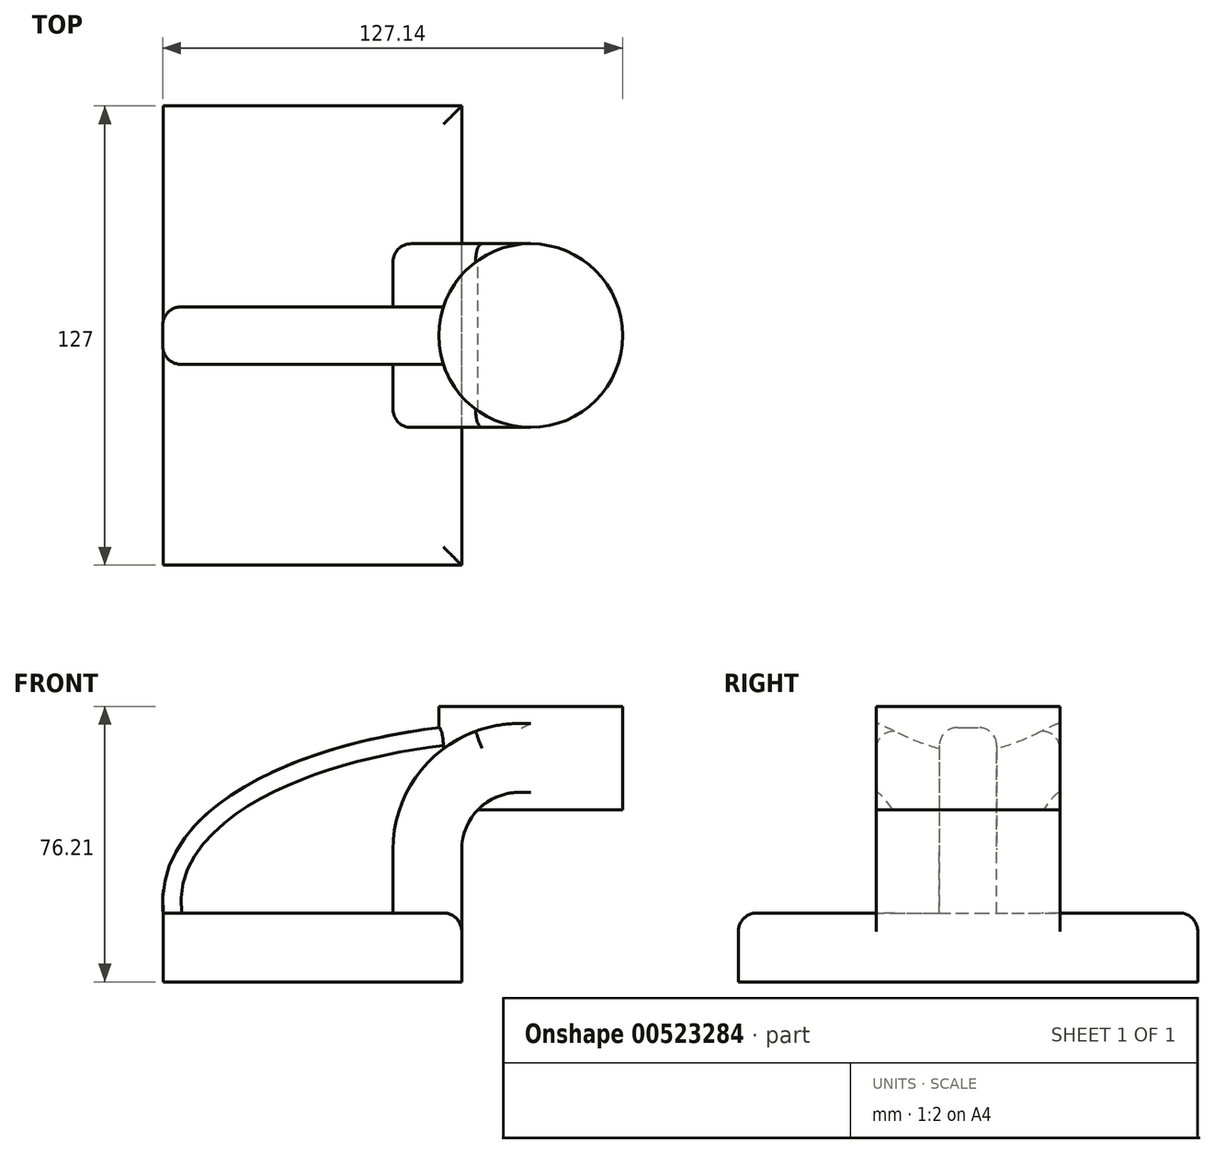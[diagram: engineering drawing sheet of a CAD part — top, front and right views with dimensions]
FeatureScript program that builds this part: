
annotation { "Feature Type Name" : "Feature", "Feature Type Description" : "" }
export const myFeature = defineFeature(function(context is Context, id is Id, definition is map)
    precondition{}
    {
        {
            var Q0;
            Q0=qCreatedBy(makeId("Front.planeOp"),FACE);
            var sketch = newSketch(context, id + "F0", { "sketchPlane" : qUnion([Q0])});
            skLineSegment(sketch, "E0.bottom", {"start": v(-41.28, -9.52) * mm, "end": v(41.28, -9.52) * mm});
            skLineSegment(sketch, "E0.top", {"start": v(-41.28, 9.53) * mm, "end": v(41.28, 9.53) * mm});
            skLineSegment(sketch, "E0.left", {"start": v(-41.27, -9.52) * mm, "end": v(-41.28, 9.53) * mm});
            skLineSegment(sketch, "E0.right", {"start": v(41.28, -9.52) * mm, "end": v(41.28, 9.53) * mm});
            skPoint(sketch, "E0.middle", {"position": v(0, 0) * mm});
            skLineSegment(sketch, "E1.bottom", {"start": v(60.32, 38.1) * mm, "end": v(111.12, 38.1) * mm});
            skLineSegment(sketch, "E1.top", {"start": v(60.32, 66.68) * mm, "end": v(111.12, 66.68) * mm});
            skLineSegment(sketch, "E1.left", {"start": v(60.32, 38.1) * mm, "end": v(60.32, 66.67) * mm});
            skLineSegment(sketch, "E1.right", {"start": v(111.13, 38.1) * mm, "end": v(111.12, 66.67) * mm});
            skPoint(sketch, "E1.middle", {"position": v(85.72, 52.39) * mm});
            skLineSegment(sketch, "E2", {"start": v(41.27, 9.53) * mm, "end": v(41.27, 27) * mm});
            skArc(sketch, "E3", {"start": v(57.15, 42.88) * mm, "mid": v(45.92, 38.23) * mm, "end": v(41.27, 27) * mm});
            skLineSegment(sketch, "E4", {"start": v(57.15, 42.88) * mm, "end": v(85.72, 42.88) * mm});
            skLineSegment(sketch, "E5.0", {"start": v(22.23, 9.53) * mm, "end": v(22.23, 27) * mm});
            skArc(sketch, "E5.1", {"start": v(57.15, 61.93) * mm, "mid": v(32.45, 51.7) * mm, "end": v(22.22, 27) * mm});
            skLineSegment(sketch, "E5.2", {"start": v(57.15, 61.93) * mm, "end": v(85.72, 61.93) * mm});
            skLineSegment(sketch, "E6", {"start": v(85.72, 61.93) * mm, "end": v(85.72, 52.39) * mm});
            skLineSegment(sketch, "E7", {"start": v(85.72, 52.39) * mm, "end": v(85.72, 42.88) * mm});
            skLineSegment(sketch, "E8", {"start": v(85.72, 66.68) * mm, "end": v(85.72, 38.1) * mm});
            skFitSpline(sketch, "E9", {"points": [v(-41.28, 9.53) * mm, v(57.15, 61.93) * mm], "startDerivative": vector(-10.2, 109.99) * mm, "endDerivative": vector(117.62, -2.77) * mm});
            skSolve(sketch);
        }
        {
            var Q0;
            Q0=makeQuery(id+"F0.imprint","IMPRINT",FACE,{"disambiguationData":[TD([[makeQuery(id+"F0.imprint","IMPRINT",EDGE,{"derivedFrom":sQuery(id+"F0.wireOp",EDGE,"E0.bottom")}),1.0]])]});
            extrude(context, id + "F1", {"entities" : qUnion([Q0]), "endBound" : BoundingType.SYMMETRIC, "depth" : 127 * mm, "offsetDistance" : 25.4 * mm});
        }
        {
            var Q0;
            {var subQ1=sQuery(id+"F0.wireOp",EDGE,"E2");Q0=makeQuery(id+"F0.imprint","IMPRINT",FACE,{"disambiguationData":[TD([[makeQuery(id+"F0.imprint","IMPRINT",EDGE,{"derivedFrom":subQ1}),1.0]])]});}
            extrude(context, id + "F2", {"entities" : qUnion([Q0]), "operationType" : NewBodyOperationType.ADD, "endBound" : BoundingType.SYMMETRIC, "depth" : 50.8 * mm, "offsetDistance" : 25.4 * mm});
        }
        {
            var Q0;
            {var subQ2=sQuery(id+"F0.wireOp",EDGE,"E5.0");Q0=makeQuery(id+"F0.imprint","IMPRINT",FACE,{"disambiguationData":[TD([[makeQuery(id+"F0.imprint","IMPRINT",EDGE,{"derivedFrom":subQ2}),1.0]])]});}
            extrude(context, id + "F3", {"entities" : qUnion([Q0]), "operationType" : NewBodyOperationType.ADD, "endBound" : BoundingType.SYMMETRIC, "depth" : 15.88 * mm, "offsetDistance" : 25.4 * mm});
        }
        {
            var Q0;
            {var subQ0=sQuery(id+"F0.wireOp",EDGE,"E1.left");var subQ1=sQuery(id+"F0.wireOp",EDGE,"E1.top");var subQ2=makeQuery(id+"F0.imprint","INTERSECT",VERTEX,{"derivedFrom":[subQ1,subQ0]});Q0=makeQuery(id+"F0.imprint","IMPRINT",FACE,{"disambiguationData":[TD([[makeQuery(id+"F0.imprint","IMPRINT",EDGE,{"disambiguationData":[TD([[subQ2,-1.0]])],"derivedFrom":subQ1}),-1.0]])]});}
            var Q1;
            {var subQ0=sQuery(id+"F0.wireOp",EDGE,"E4");var subQ1=sQuery(id+"F0.wireOp",EDGE,"E1.left");var subQ2=makeQuery(id+"F0.imprint","INTERSECT",VERTEX,{"derivedFrom":[subQ1,subQ0]});Q1=makeQuery(id+"F0.imprint","IMPRINT",FACE,{"disambiguationData":[TD([[makeQuery(id+"F0.imprint","IMPRINT",EDGE,{"disambiguationData":[TD([[subQ2,-1.0]])],"derivedFrom":subQ1}),-1.0]])]});}
            var Q2;
            {var subQ0=sQuery(id+"F0.wireOp",EDGE,"E1.left");var subQ1=sQuery(id+"F0.wireOp",EDGE,"E1.bottom");var subQ2=makeQuery(id+"F0.imprint","INTERSECT",VERTEX,{"derivedFrom":[subQ1,subQ0]});Q2=makeQuery(id+"F0.imprint","IMPRINT",FACE,{"disambiguationData":[TD([[makeQuery(id+"F0.imprint","IMPRINT",EDGE,{"disambiguationData":[TD([[subQ2,-1.0]])],"derivedFrom":subQ1}),1.0]])]});}
            var Q3;
            Q3=sQuery(id+"F0.wireOp",EDGE,"E1.left");
            revolve(context, id + "F4", {"operationType" : NewBodyOperationType.ADD, "entities" : qUnion([Q0, Q1, Q2]), "axis" : qUnion([Q3]), "revolveType" : RevolveType.FULL});
        }
        {
            var Q0;
            Q0=makeQuery(id+"F3.opExtrude","CAP_EDGE",EDGE,{"disambiguationData":[OSD([sQuery(id+"F0.wireOp",EDGE,"E9")])],"isStart":false});
            var Q1;
            Q1=makeQuery(id+"F3.opExtrude","CAP_EDGE",EDGE,{"disambiguationData":[OSD([sQuery(id+"F0.wireOp",EDGE,"E9")])],"isStart":true});
            var Q2;
            Q2=makeQuery(id+"F2.opExtrude","CAP_EDGE",EDGE,{"disambiguationData":[OSD([sQuery(id+"F0.wireOp",EDGE,"E5.1")])],"isStart":true});
            var Q3;
            Q3=makeQuery(id+"F2.opExtrude","CAP_EDGE",EDGE,{"disambiguationData":[OSD([sQuery(id+"F0.wireOp",EDGE,"E5.0")])],"isStart":true});
            var Q4;
            Q4=makeQuery(id+"F2.opExtrude","CAP_EDGE",EDGE,{"disambiguationData":[OSD([sQuery(id+"F0.wireOp",EDGE,"E5.1")])],"isStart":false});
            var Q5;
            Q5=makeQuery(id+"F2.opExtrude","CAP_EDGE",EDGE,{"disambiguationData":[OSD([sQuery(id+"F0.wireOp",EDGE,"E5.0")])],"isStart":false});
            fillet(context, id + "F5", {"entities" : qUnion([Q0, Q1, Q2, Q3, Q4, Q5]), "radius" : 5.08 * mm, "tangentPropagation" : true, "allowEdgeOverflow" : false});
        }
        {
            var Q0;
            {var subQ0=sQuery(id+"F0.wireOp",EDGE,"E2");var subQ1=sQuery(id+"F0.wireOp",EDGE,"E0.top");var subQ2=sQuery(id+"F0.wireOp",EDGE,"E0.right");Q0=makeQuery(id+"F2.boolean.opBoolean","SPLIT",EDGE,{"disambiguationData":[TD([makeQuery(id+"F1.opExtrude","CAP_FACE",FACE,{"disambiguationData":[OSD([sQuery(id+"F0.wireOp",EDGE,"E0.bottom"),subQ1,sQuery(id+"F0.wireOp",EDGE,"E0.left"),subQ2])],"isStart":true})])],"derivedFrom":makeQuery(id+"F1.opExtrude","SWEPT_EDGE",EDGE,{"disambiguationData":[OSD([subQ1,subQ2,subQ0])]})});}
            var Q1;
            Q1=makeQuery(id+"F1.opExtrude","CAP_EDGE",EDGE,{"disambiguationData":[OSD([sQuery(id+"F0.wireOp",EDGE,"E0.top")])],"isStart":true});
            var Q2;
            {var subQ0=sQuery(id+"F0.wireOp",EDGE,"E0.right");var subQ1=sQuery(id+"F0.wireOp",EDGE,"E2");var subQ2=sQuery(id+"F0.wireOp",EDGE,"E0.top");Q2=makeQuery(id+"F2.boolean.opBoolean","SPLIT",EDGE,{"disambiguationData":[TD([makeQuery(id+"F1.opExtrude","CAP_FACE",FACE,{"disambiguationData":[OSD([sQuery(id+"F0.wireOp",EDGE,"E0.bottom"),subQ2,sQuery(id+"F0.wireOp",EDGE,"E0.left"),subQ0])],"isStart":false})])],"derivedFrom":makeQuery(id+"F1.opExtrude","SWEPT_EDGE",EDGE,{"disambiguationData":[OSD([subQ2,subQ0,subQ1])]})});}
            var Q3;
            Q3=makeQuery(id+"F1.opExtrude","CAP_EDGE",EDGE,{"disambiguationData":[OSD([sQuery(id+"F0.wireOp",EDGE,"E0.top")])],"isStart":false});
            fillet(context, id + "F6", {"entities" : qUnion([Q0, Q1, Q2, Q3]), "radius" : 5.08 * mm, "tangentPropagation" : true, "allowEdgeOverflow" : false});
        }
    });
